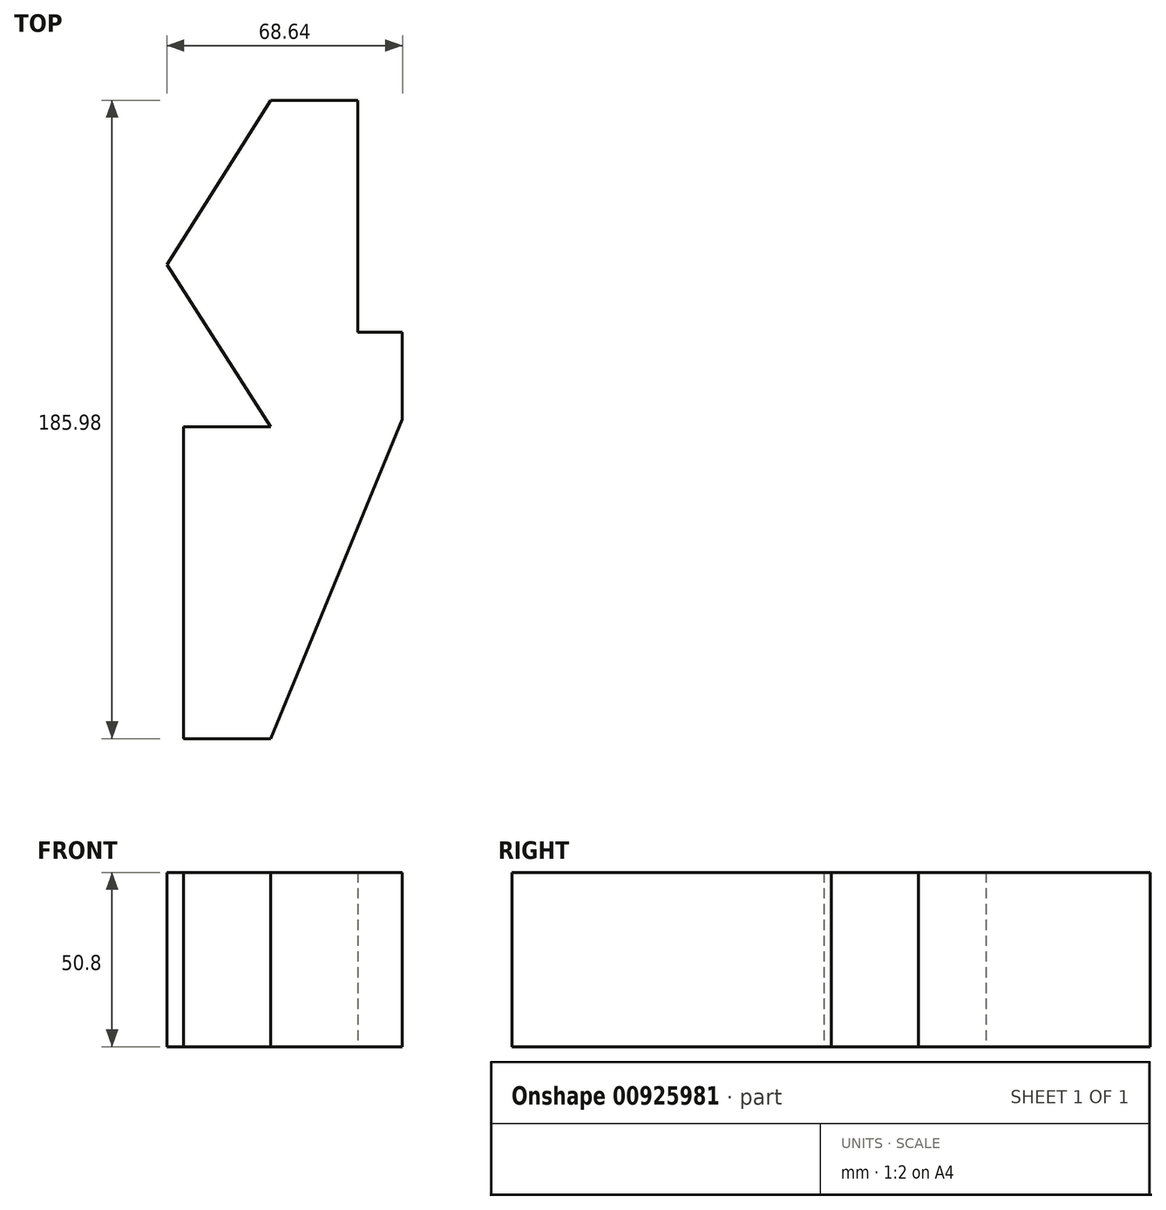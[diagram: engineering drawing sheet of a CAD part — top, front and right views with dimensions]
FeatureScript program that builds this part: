
annotation { "Feature Type Name" : "Feature", "Feature Type Description" : "" }
export const myFeature = defineFeature(function(context is Context, id is Id, definition is map)
    precondition{}
    {
        {
            var Q0;
            Q0=qCreatedBy(makeId("Top.planeOp"),FACE);
            var sketch = newSketch(context, id + "F0", { "sketchPlane" : qUnion([Q0])});
            skLineSegment(sketch, "E0", {"start": v(0, 86.66) * mm, "end": v(1.57, 6.65) * mm});
            skLineSegment(sketch, "E1", {"start": v(1.57, 6.65) * mm, "end": v(51.86, 5.7) * mm});
            skLineSegment(sketch, "E2", {"start": v(51.86, 5.7) * mm, "end": v(-0.17, 87.35) * mm});
            skLineSegment(sketch, "E3", {"start": v(-0.17, 87.35) * mm, "end": v(30, 135.17) * mm});
            skLineSegment(sketch, "E4", {"start": v(30, 135.17) * mm, "end": v(30, -50.81) * mm});
            skLineSegment(sketch, "E5", {"start": v(30, -50.81) * mm, "end": v(68.47, 42.18) * mm});
            skPoint(sketch, "E5.endSnap0", {"position": v(30, 42.18) * mm});
            skLineSegment(sketch, "E6", {"start": v(68.47, 42.18) * mm, "end": v(30, 42.18) * mm});
            skSolve(sketch);
        }
        {
            var Q0;
            Q0 = qSketchRegion(id + "F0", true);
            extrude(context, id + "F1", {"entities" : qUnion([Q0]), "depth" : 25.4 * mm, "offsetDistance" : 25.4 * mm});
        }
        {
            var Q0;
            {var subQ0=sQuery(id+"F0.wireOp",EDGE,"E4");Q0=makeQuery(id+"F1.opExtrude","SWEPT_FACE",FACE,{"disambiguationData":[OSD([subQ0]),TDD([makeQuery(id+"F0.imprint","IMPRINT",EDGE,{"disambiguationData":[TD([[makeQuery(id+"F0.imprint","INTERSECT",VERTEX,{"derivedFrom":[sQuery(id+"F0.wireOp",EDGE,"E3"),subQ0]}),-1.0]])],"derivedFrom":subQ0})])]});}
            extrude(context, id + "F2", {"entities" : qUnion([Q0]), "operationType" : NewBodyOperationType.ADD, "depth" : 25.4 * mm, "offsetDistance" : 25.4 * mm});
        }
        {
            var Q0;
            {var subQ0=sQuery(id+"F0.wireOp",EDGE,"E4");var subQ1=sQuery(id+"F0.wireOp",EDGE,"E3");var subQ2=sQuery(id+"F0.wireOp",EDGE,"E6");Q0=makeQuery(id+"F2.boolean.opBoolean","MERGE",FACE,{"derivedFrom":[makeQuery(id+"F1.opExtrude","CAP_FACE",FACE,{"disambiguationData":[OSD([sQuery(id+"F0.wireOp",EDGE,"E2"),subQ1,subQ0,sQuery(id+"F0.wireOp",EDGE,"E5"),subQ2])],"isStart":true}),makeQuery(id+"F2.opExtrude","SWEPT_FACE",FACE,{"disambiguationData":[OSD([subQ0]),TDD([makeQuery(id+"F1.opExtrude","CAP_EDGE",EDGE,{"disambiguationData":[OSD([subQ0]),TDD([makeQuery(id+"F0.imprint","IMPRINT",EDGE,{"disambiguationData":[TD([[makeQuery(id+"F0.imprint","INTERSECT",VERTEX,{"derivedFrom":[subQ1,subQ0]}),-1.0]])],"derivedFrom":subQ0})])],"isStart":true})])]})]});}
            extrude(context, id + "F3", {"entities" : qUnion([Q0]), "operationType" : NewBodyOperationType.ADD, "depth" : 25.4 * mm, "offsetDistance" : 25.4 * mm});
        }
        {
            var Q0;
            {var subQ0=sQuery(id+"F0.wireOp",EDGE,"E6");Q0=makeQuery(id+"F3.boolean.opBoolean","MERGE",FACE,{"derivedFrom":[makeQuery(id+"F1.opExtrude","SWEPT_FACE",FACE,{"disambiguationData":[OSD([subQ0])]}),makeQuery(id+"F3.opExtrude","SWEPT_FACE",FACE,{"disambiguationData":[OSD([subQ0])]})]});}
            extrude(context, id + "F4", {"entities" : qUnion([Q0]), "operationType" : NewBodyOperationType.ADD, "depth" : 25.4 * mm, "offsetDistance" : 25.4 * mm});
        }
        {
            var Q0;
            {var subQ0=sQuery(id+"F0.wireOp",EDGE,"E4");var subQ1=makeQuery(id+"F0.imprint","INTERSECT",VERTEX,{"derivedFrom":[sQuery(id+"F0.wireOp",EDGE,"E1"),subQ0]});var subQ2=makeQuery(id+"F0.imprint","IMPRINT",EDGE,{"disambiguationData":[TD([[makeQuery(id+"F0.imprint","INTERSECT",VERTEX,{"derivedFrom":[subQ0,sQuery(id+"F0.wireOp",EDGE,"E5")]}),1.0]])],"derivedFrom":subQ0});var subQ3=makeQuery(id+"F0.imprint","IMPRINT",EDGE,{"disambiguationData":[TD([[subQ1,1.0]])],"derivedFrom":subQ0});Q0=makeQuery(id+"F3.boolean.opBoolean","MERGE",FACE,{"derivedFrom":[makeQuery(id+"F1.opExtrude","SWEPT_FACE",FACE,{"disambiguationData":[OSD([subQ0]),TDD([subQ3,subQ2])]}),makeQuery(id+"F3.opExtrude","SWEPT_FACE",FACE,{"disambiguationData":[OSD([subQ0]),TDD([makeQuery(id+"F1.opExtrude","CAP_EDGE",EDGE,{"disambiguationData":[OSD([subQ0]),TDD([subQ3,subQ2])],"isStart":true})])]})]});}
            extrude(context, id + "F5", {"entities" : qUnion([Q0]), "operationType" : NewBodyOperationType.ADD, "depth" : 25.4 * mm, "offsetDistance" : 25.4 * mm});
        }
    });
